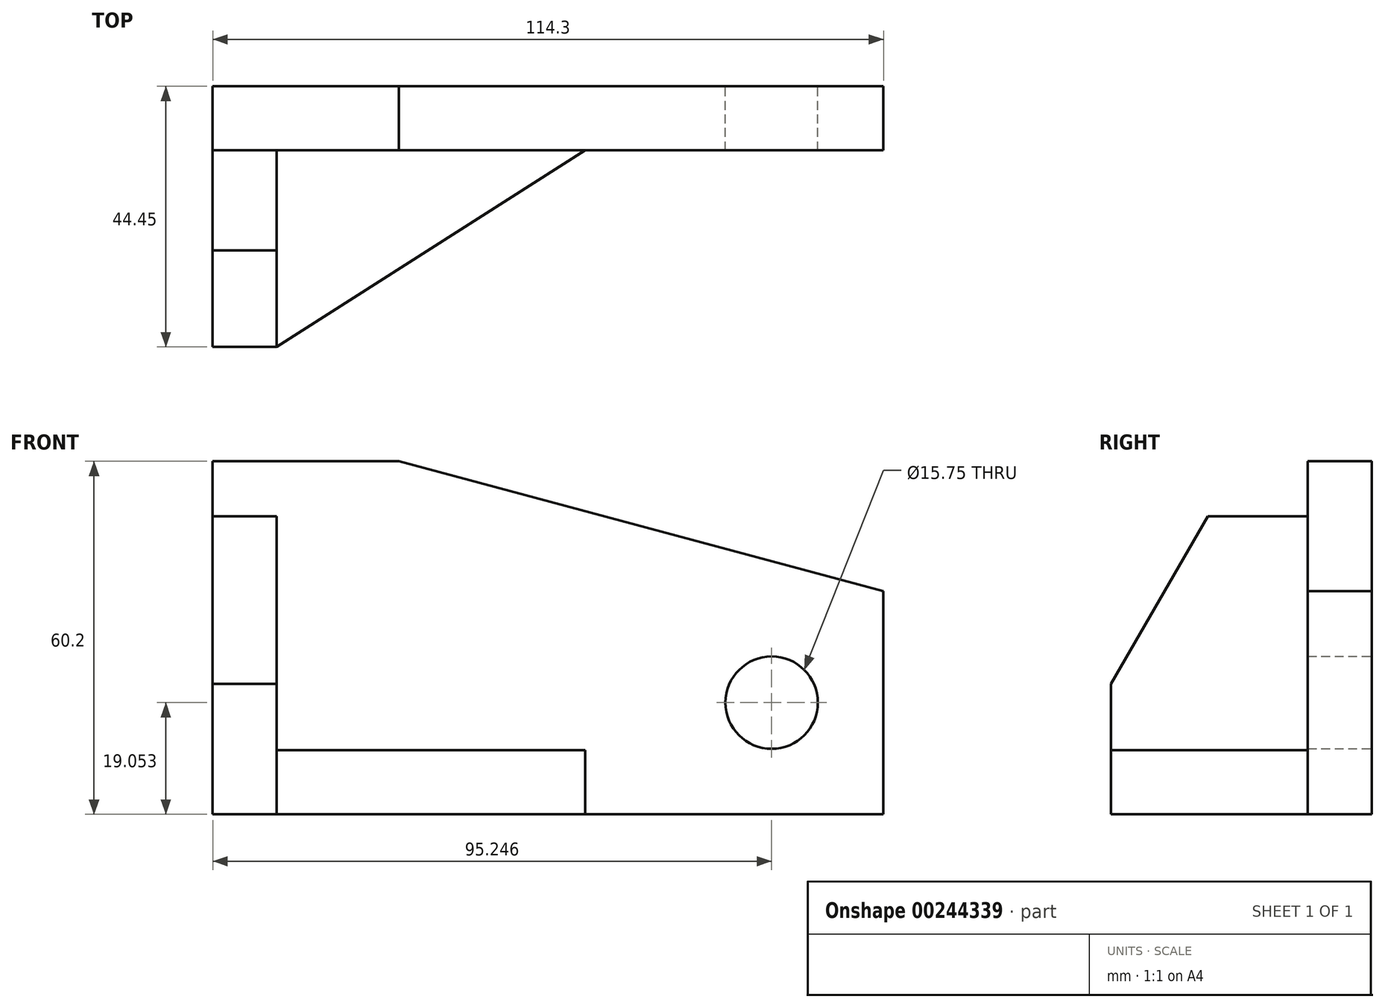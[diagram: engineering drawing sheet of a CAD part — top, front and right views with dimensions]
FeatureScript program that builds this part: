
annotation { "Feature Type Name" : "Feature", "Feature Type Description" : "" }
export const myFeature = defineFeature(function(context is Context, id is Id, definition is map)
    precondition{}
    {
        {
            var Q0;
            Q0=qCreatedBy(makeId("Front.planeOp"),FACE);
            var sketch = newSketch(context, id + "F0", { "sketchPlane" : qUnion([Q0])});
            skLineSegment(sketch, "E0.bottom", {"start": v(-76.61, 76.48) * mm, "end": v(37.69, 76.48) * mm});
            skLineSegment(sketch, "E0.top", {"start": v(-76.61, 16.28) * mm, "end": v(37.69, 16.28) * mm});
            skLineSegment(sketch, "E0.left", {"start": v(-76.61, 76.48) * mm, "end": v(-76.61, 16.28) * mm});
            skLineSegment(sketch, "E0.right", {"start": v(37.69, 76.48) * mm, "end": v(37.69, 16.28) * mm});
            skCircle(sketch, "E1", {"center": v(18.64, 35.33) * mm, "radius": 7.87 * mm});
            skLineSegment(sketch, "E2", {"start": v(-76.61, 16.28) * mm, "end": v(-13.11, 16.28) * mm});
            skLineSegment(sketch, "E3", {"start": v(-13.11, 16.28) * mm, "end": v(-13.11, 27.2) * mm});
            skLineSegment(sketch, "E4", {"start": v(-65.7, 27.2) * mm, "end": v(-65.7, 16.28) * mm});
            skLineSegment(sketch, "E5", {"start": v(-65.7, 27.2) * mm, "end": v(-13.11, 27.2) * mm});
            skLineSegment(sketch, "E6", {"start": v(-65.7, 16.28) * mm, "end": v(-65.7, 38.38) * mm});
            skLineSegment(sketch, "E7", {"start": v(-65.7, 38.38) * mm, "end": v(-76.61, 38.38) * mm});
            skLineSegment(sketch, "E8", {"start": v(-76.61, 38.38) * mm, "end": v(-76.61, 16.28) * mm});
            skLineSegment(sketch, "E9", {"start": v(-65.7, 16.28) * mm, "end": v(-65.7, 67.08) * mm});
            skLineSegment(sketch, "E10", {"start": v(-65.7, 67.08) * mm, "end": v(-76.61, 67.08) * mm});
            skSolve(sketch);
        }
        {
            var Q0;
            {var subQ1=sQuery(id+"F0.wireOp",EDGE,"E0.bottom");Q0=makeQuery(id+"F0.imprint","IMPRINT",FACE,{"disambiguationData":[TD([[makeQuery(id+"F0.imprint","IMPRINT",EDGE,{"derivedFrom":subQ1}),-1.0]])]});}
            extrude(context, id + "F1", {"entities" : qUnion([Q0]), "depth" : 10.92 * mm});
        }
        {
            var Q0;
            {var subQ5=sQuery(id+"F0.wireOp",EDGE,"E7");Q0=makeQuery(id+"F0.imprint","IMPRINT",FACE,{"disambiguationData":[TD([[makeQuery(id+"F0.imprint","IMPRINT",EDGE,{"derivedFrom":subQ5}),1.0]])]});}
            extrude(context, id + "F2", {"entities" : qUnion([Q0]), "operationType" : NewBodyOperationType.ADD, "depth" : 44.45 * mm});
        }
        {
            var Q0;
            {var subQ0=sQuery(id+"F0.wireOp",EDGE,"E7");Q0=makeQuery(id+"F0.imprint","IMPRINT",FACE,{"disambiguationData":[TD([[makeQuery(id+"F0.imprint","IMPRINT",EDGE,{"derivedFrom":subQ0}),-1.0]])]});}
            extrude(context, id + "F3", {"entities" : qUnion([Q0]), "operationType" : NewBodyOperationType.ADD, "depth" : 44.45 * mm});
        }
        {
            var Q0;
            {var subQ0=sQuery(id+"F0.wireOp",EDGE,"E3");Q0=makeQuery(id+"F0.imprint","IMPRINT",FACE,{"disambiguationData":[TD([[makeQuery(id+"F0.imprint","IMPRINT",EDGE,{"derivedFrom":subQ0}),1.0]])]});}
            extrude(context, id + "F4", {"entities" : qUnion([Q0]), "operationType" : NewBodyOperationType.ADD, "depth" : 44.45 * mm});
        }
        {
            var Q0;
            {var subQ0=sQuery(id+"F0.wireOp",EDGE,"E9");Q0=makeQuery(id+"F3.boolean.opBoolean","MERGE",FACE,{"derivedFrom":[makeQuery(id+"F2.opExtrude","SWEPT_FACE",FACE,{"disambiguationData":[OSD([subQ0])]}),makeQuery(id+"F3.opExtrude","SWEPT_FACE",FACE,{"disambiguationData":[OSD([subQ0])]})]});}
            var sketch = newSketch(context, id + "F5", { "sketchPlane" : qUnion([Q0])});
            skLineSegment(sketch, "E11", {"start": v(-44.45, 38.53) * mm, "end": v(-27.96, 67.08) * mm});
            skSolve(sketch);
        }
        {
            var Q0;
            {var subQ0=sQuery(id+"F5.wireOp",EDGE,"E11");Q0=makeQuery(id+"F5.imprint","IMPRINT",FACE,{"disambiguationData":[TD([[makeQuery(id+"F5.imprint","IMPRINT",EDGE,{"derivedFrom":subQ0}),1.0]])]});}
            extrude(context, id + "F6", {"entities" : qUnion([Q0]), "operationType" : NewBodyOperationType.REMOVE, "endBound" : BoundingType.THROUGH_ALL, "oppositeDirection" : true, "depth" : 25.4 * mm});
        }
        {
            var Q0;
            Q0=makeQuery(id+"F4.opExtrude","SWEPT_FACE",FACE,{"disambiguationData":[OSD([sQuery(id+"F0.wireOp",EDGE,"E5")])]});
            var sketch = newSketch(context, id + "F7", { "sketchPlane" : qUnion([Q0])});
            skLineSegment(sketch, "E12", {"start": v(-65.7, -44.45) * mm, "end": v(-13.11, -10.92) * mm});
            skSolve(sketch);
        }
        {
            var Q0;
            Q0=makeQuery(id+"F7.imprint","IMPRINT",FACE,{"disambiguationData":[TD([[makeQuery(id+"F7.imprint","IMPRINT",EDGE,{"derivedFrom":sQuery(id+"F7.wireOp",EDGE,"E12")}),-1.0]])]});
            extrude(context, id + "F8", {"entities" : qUnion([Q0]), "operationType" : NewBodyOperationType.REMOVE, "endBound" : BoundingType.THROUGH_ALL, "oppositeDirection" : true, "depth" : 25.4 * mm});
        }
        {
            var Q0;
            Q0=makeQuery(id+"F1.opExtrude","CAP_FACE",FACE,{"disambiguationData":[OSD([sQuery(id+"F0.wireOp",EDGE,"E0.bottom"),sQuery(id+"F0.wireOp",EDGE,"E0.top"),sQuery(id+"F0.wireOp",EDGE,"E0.left"),sQuery(id+"F0.wireOp",EDGE,"E0.right"),sQuery(id+"F0.wireOp",EDGE,"E1"),sQuery(id+"F0.wireOp",EDGE,"E3"),sQuery(id+"F0.wireOp",EDGE,"E5"),sQuery(id+"F0.wireOp",EDGE,"E9"),sQuery(id+"F0.wireOp",EDGE,"E10")])],"isStart":false});
            var sketch = newSketch(context, id + "F9", { "sketchPlane" : qUnion([Q0])});
            skLineSegment(sketch, "E13", {"start": v(-76.61, 76.48) * mm, "end": v(-44.86, 76.48) * mm});
            skLineSegment(sketch, "E14", {"start": v(-44.86, 76.48) * mm, "end": v(37.69, 54.36) * mm});
            skSolve(sketch);
        }
        {
            var Q0;
            {var subQ0=sQuery(id+"F9.wireOp",EDGE,"E14");Q0=makeQuery(id+"F9.imprint","IMPRINT",FACE,{"disambiguationData":[TD([[makeQuery(id+"F9.imprint","IMPRINT",EDGE,{"derivedFrom":subQ0}),1.0]])]});}
            extrude(context, id + "F10", {"entities" : qUnion([Q0]), "operationType" : NewBodyOperationType.REMOVE, "endBound" : BoundingType.THROUGH_ALL, "oppositeDirection" : true, "depth" : 25.4 * mm});
        }
    });
